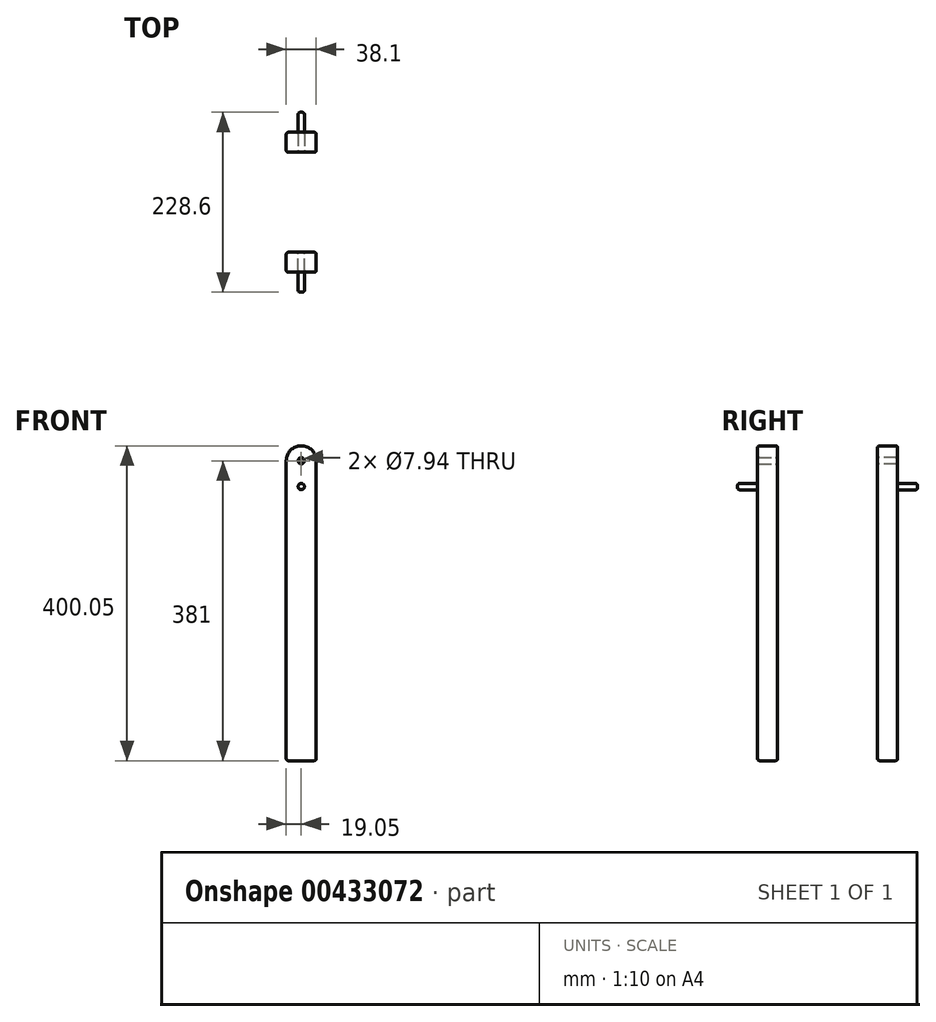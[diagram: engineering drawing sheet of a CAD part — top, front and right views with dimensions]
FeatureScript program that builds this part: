
annotation { "Feature Type Name" : "Feature", "Feature Type Description" : "" }
export const myFeature = defineFeature(function(context is Context, id is Id, definition is map)
    precondition{}
    {
        {
            var Q0;
            Q0=qCreatedBy(makeId("Front.planeOp"),FACE);
            var sketch = newSketch(context, id + "F0", { "sketchPlane" : qUnion([Q0])});
            skLineSegment(sketch, "E0.bottom", {"start": v(0, 0) * mm, "end": v(38.1, 0) * mm});
            skLineSegment(sketch, "E0.left", {"start": v(0, 0) * mm, "end": v(0, 381) * mm});
            skLineSegment(sketch, "E0.right", {"start": v(38.1, 0) * mm, "end": v(38.1, 381) * mm});
            skArc(sketch, "E1", {"start": v(0, 381) * mm, "mid": v(19.05, 400.05) * mm, "end": v(38.1, 381) * mm});
            skCircle(sketch, "E2", {"center": v(19.05, 381) * mm, "radius": 3.97 * mm});
            skCircle(sketch, "E3", {"center": v(19.05, 348.14) * mm, "radius": 3.97 * mm});
            skSolve(sketch);
        }
        {
            var Q0;
            Q0=makeQuery(id+"F0.imprint","IMPRINT",FACE,{"disambiguationData":[TD([[makeQuery(id+"F0.imprint","IMPRINT",EDGE,{"derivedFrom":sQuery(id+"F0.wireOp",EDGE,"E3")}),1.0]])]});
            extrude(context, id + "F1", {"entities" : qUnion([Q0]), "depth" : 50.8 * mm});
        }
        {
            var Q0;
            Q0=makeQuery(id+"F0.imprint","IMPRINT",FACE,{"disambiguationData":[TD([[makeQuery(id+"F0.imprint","IMPRINT",EDGE,{"derivedFrom":sQuery(id+"F0.wireOp",EDGE,"E0.bottom")}),1.0]])]});
            extrude(context, id + "F2", {"entities" : qUnion([Q0]), "operationType" : NewBodyOperationType.ADD, "depth" : 25.4 * mm});
        }
        {
            var Q0;
            Q0=makeQuery(id+"F1.opExtrude","SWEPT_FACE",FACE,{"disambiguationData":[OSD([sQuery(id+"F0.wireOp",EDGE,"E3")])]});
            var Q1;
            Q1=makeQuery(id+"F2.opExtrude","CAP_FACE",FACE,{"disambiguationData":[OSD([sQuery(id+"F0.wireOp",EDGE,"E0.bottom"),sQuery(id+"F0.wireOp",EDGE,"E0.left"),sQuery(id+"F0.wireOp",EDGE,"E0.right"),sQuery(id+"F0.wireOp",EDGE,"E1"),sQuery(id+"F0.wireOp",EDGE,"E2"),sQuery(id+"F0.wireOp",EDGE,"E3")])],"isStart":false});
            var Q2;
            Q2=makeQuery(id+"F2.opExtrude","SWEPT_FACE",FACE,{"disambiguationData":[OSD([sQuery(id+"F0.wireOp",EDGE,"E1")])]});
            var Q3;
            Q3=makeQuery(id+"F2.opExtrude","SWEPT_FACE",FACE,{"disambiguationData":[OSD([sQuery(id+"F0.wireOp",EDGE,"E0.left")])]});
            var Q4;
            Q4=makeQuery(id+"F2.opExtrude","SWEPT_FACE",FACE,{"disambiguationData":[OSD([sQuery(id+"F0.wireOp",EDGE,"E2")])]});
            var Q5;
            Q5=makeQuery(id+"F2.opExtrude","SWEPT_FACE",FACE,{"disambiguationData":[OSD([sQuery(id+"F0.wireOp",EDGE,"E0.right")])]});
            var Q6;
            Q6=makeQuery(id+"F1.opExtrude","CAP_FACE",FACE,{"disambiguationData":[OSD([sQuery(id+"F0.wireOp",EDGE,"E3")])],"isStart":false});
            var Q7;
            Q7=makeQuery(id+"F2.opExtrude","SWEPT_FACE",FACE,{"disambiguationData":[OSD([sQuery(id+"F0.wireOp",EDGE,"E0.bottom")])]});
            var Q8;
            Q8=makeQuery(id+"F2.opExtrude","CAP_EDGE",EDGE,{"disambiguationData":[OSD([sQuery(id+"F0.wireOp",EDGE,"E1")])],"isStart":false});
            var Q9;
            Q9=makeQuery(id+"F2.opExtrude","SWEPT_EDGE",EDGE,{"disambiguationData":[OSD([sQuery(id+"F0.wireOp",EDGE,"E0.right"),sQuery(id+"F0.wireOp",EDGE,"E1")])]});
            var Q10;
            Q10=makeQuery(id+"F2.opExtrude","CAP_EDGE",EDGE,{"disambiguationData":[OSD([sQuery(id+"F0.wireOp",EDGE,"E0.right")])],"isStart":true});
            var Q11;
            Q11=makeQuery(id+"F2.opExtrude","CAP_EDGE",EDGE,{"disambiguationData":[OSD([sQuery(id+"F0.wireOp",EDGE,"E3")])],"isStart":false});
            var Q12;
            Q12=makeQuery(id+"F2.opExtrude","CAP_EDGE",EDGE,{"disambiguationData":[OSD([sQuery(id+"F0.wireOp",EDGE,"E0.bottom")])],"isStart":false});
            var Q13;
            Q13=makeQuery(id+"F2.opExtrude","CAP_EDGE",EDGE,{"disambiguationData":[OSD([sQuery(id+"F0.wireOp",EDGE,"E0.left")])],"isStart":false});
            var Q14;
            {var subQ0=sQuery(id+"F0.wireOp",EDGE,"E3");Q14=makeQuery(id+"F2.boolean.opBoolean","MERGE",FACE,{"derivedFrom":[makeQuery(id+"F1.opExtrude","CAP_FACE",FACE,{"disambiguationData":[OSD([subQ0])],"isStart":true}),makeQuery(id+"F2.opExtrude","CAP_FACE",FACE,{"disambiguationData":[OSD([sQuery(id+"F0.wireOp",EDGE,"E0.bottom"),sQuery(id+"F0.wireOp",EDGE,"E0.left"),sQuery(id+"F0.wireOp",EDGE,"E0.right"),sQuery(id+"F0.wireOp",EDGE,"E1"),sQuery(id+"F0.wireOp",EDGE,"E2"),subQ0])],"isStart":true})]});}
            var Q15;
            Q15=makeQuery(id+"F2.opExtrude","CAP_EDGE",EDGE,{"disambiguationData":[OSD([sQuery(id+"F0.wireOp",EDGE,"E0.right")])],"isStart":false});
            var Q16;
            Q16=makeQuery(id+"F2.opExtrude","CAP_EDGE",EDGE,{"disambiguationData":[OSD([sQuery(id+"F0.wireOp",EDGE,"E0.bottom")])],"isStart":true});
            var Q17;
            Q17=makeQuery(id+"F2.opExtrude","SWEPT_EDGE",EDGE,{"disambiguationData":[OSD([sQuery(id+"F0.wireOp",EDGE,"E0.bottom"),sQuery(id+"F0.wireOp",EDGE,"E0.right")])]});
            var Q18;
            Q18=makeQuery(id+"F2.opExtrude","SWEPT_EDGE",EDGE,{"disambiguationData":[OSD([sQuery(id+"F0.wireOp",EDGE,"E0.left"),sQuery(id+"F0.wireOp",EDGE,"E1")])]});
            var Q19;
            Q19=makeQuery(id+"F2.opExtrude","CAP_EDGE",EDGE,{"disambiguationData":[OSD([sQuery(id+"F0.wireOp",EDGE,"E0.left")])],"isStart":true});
            var Q20;
            Q20=makeQuery(id+"F2.opExtrude","CAP_EDGE",EDGE,{"disambiguationData":[OSD([sQuery(id+"F0.wireOp",EDGE,"E2")])],"isStart":false});
            var Q21;
            Q21=makeQuery(id+"F2.opExtrude","SWEPT_EDGE",EDGE,{"disambiguationData":[OSD([sQuery(id+"F0.wireOp",EDGE,"E0.bottom"),sQuery(id+"F0.wireOp",EDGE,"E0.left")])]});
            var Q22;
            Q22=makeQuery(id+"F1.opExtrude","CAP_EDGE",EDGE,{"disambiguationData":[OSD([sQuery(id+"F0.wireOp",EDGE,"E3")])],"isStart":false});
            var Q23;
            Q23=makeQuery(id+"F2.opExtrude","CAP_EDGE",EDGE,{"disambiguationData":[OSD([sQuery(id+"F0.wireOp",EDGE,"E2")])],"isStart":true});
            var Q24;
            Q24=makeQuery(id+"F2.opExtrude","CAP_EDGE",EDGE,{"disambiguationData":[OSD([sQuery(id+"F0.wireOp",EDGE,"E1")])],"isStart":true});
            fillet(context, id + "F3", {"entities" : qUnion([Q0, Q1, Q2, Q3, Q4, Q5, Q6, Q7, Q8, Q9, Q10, Q11, Q12, Q13, Q14, Q15, Q16, Q17, Q18, Q19, Q20, Q21, Q22, Q23, Q24]), "radius" : 2.54 * mm, "tangentPropagation" : true, "allowEdgeOverflow" : false});
        }
        {
            var Q0;
            Q0=makeQuery(id+"F1.opExtrude","SWEPT_BODY",BODY,{"disambiguationData":[OSD([sQuery(id+"F0.wireOp",EDGE,"E3")])]});
            transform(context, id + "F4", {"entities" : qUnion([Q0]), "transformType" : TransformType.TRANSLATION_3D, "dx" : 0 * mm, "dy" : 127 * mm, "dz" : 0 * mm, "makeCopy" : true});
        }
        {
            var Q0;
            Q0=makeQuery(id+"F4.opPattern","COPY",BODY,{"derivedFrom":makeQuery(id+"F1.opExtrude","SWEPT_BODY",BODY,{"disambiguationData":[OSD([sQuery(id+"F0.wireOp",EDGE,"E3")])]}),"instanceName":"1"});
            var Q1;
            {var subQ0=sQuery(id+"F0.wireOp",EDGE,"E3");Q1=makeQuery(id+"F4.opPattern","COPY",FACE,{"derivedFrom":makeQuery(id+"F2.boolean.opBoolean","MERGE",FACE,{"derivedFrom":[makeQuery(id+"F1.opExtrude","CAP_FACE",FACE,{"disambiguationData":[OSD([subQ0])],"isStart":true}),makeQuery(id+"F2.opExtrude","CAP_FACE",FACE,{"disambiguationData":[OSD([sQuery(id+"F0.wireOp",EDGE,"E0.bottom"),sQuery(id+"F0.wireOp",EDGE,"E0.left"),sQuery(id+"F0.wireOp",EDGE,"E0.right"),sQuery(id+"F0.wireOp",EDGE,"E1"),sQuery(id+"F0.wireOp",EDGE,"E2"),subQ0])],"isStart":true})]}),"instanceName":"1"});}
            mirror(context, id + "F5", {"entities" : qUnion([Q0]), "mirrorPlane" : qUnion([Q1])});
        }
        {
            var Q0;
            Q0=makeQuery(id+"F4.opPattern","COPY",BODY,{"derivedFrom":makeQuery(id+"F1.opExtrude","SWEPT_BODY",BODY,{"disambiguationData":[OSD([sQuery(id+"F0.wireOp",EDGE,"E3")])]}),"instanceName":"1"});
            deleteBodies(context, id + "F6", {"entities" : qUnion([Q0])});
        }
    });
